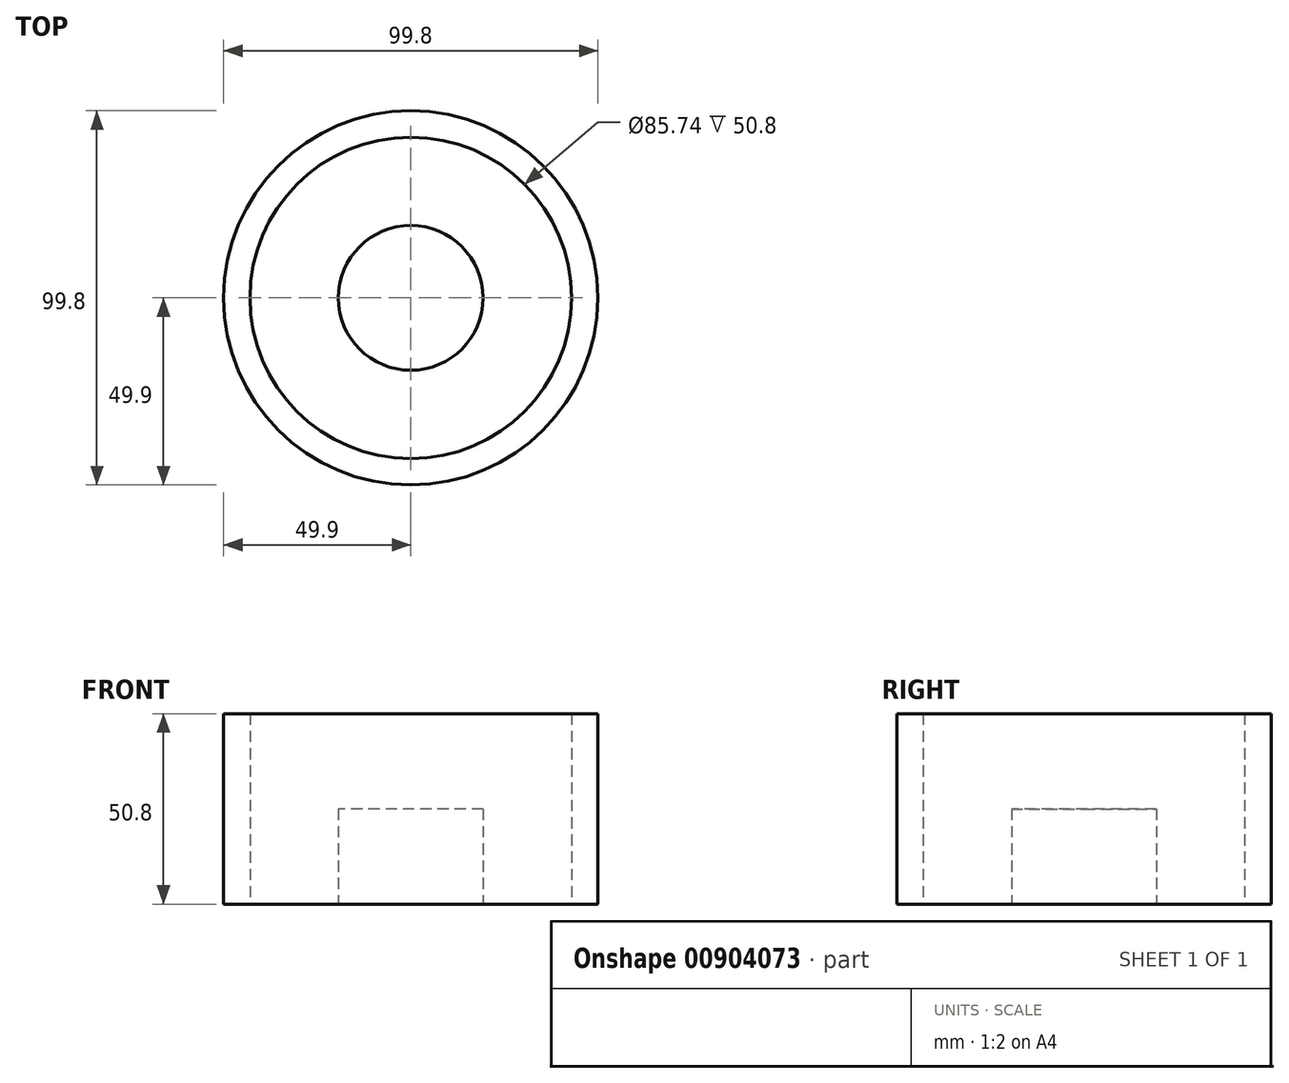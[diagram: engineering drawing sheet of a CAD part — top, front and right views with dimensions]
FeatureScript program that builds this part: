
annotation { "Feature Type Name" : "Feature", "Feature Type Description" : "" }
export const myFeature = defineFeature(function(context is Context, id is Id, definition is map)
    precondition{}
    {
        {
            var Q0;
            Q0=qCreatedBy(makeId("Top.planeOp"),FACE);
            var sketch = newSketch(context, id + "F0", { "sketchPlane" : qUnion([Q0])});
            skCircle(sketch, "E0", {"center": v(0, 0) * mm, "radius": 49.9 * mm});
            skCircle(sketch, "E1", {"center": v(0, 0) * mm, "radius": 42.87 * mm});
            skCircle(sketch, "E2", {"center": v(0, 0) * mm, "radius": 41.05 * mm});
            skCircle(sketch, "E3", {"center": v(0, 0) * mm, "radius": 16.03 * mm});
            skLineSegment(sketch, "E4", {"start": v(-9.86, -12.64) * mm, "end": v(-9.86, -27.85) * mm});
            skLineSegment(sketch, "E5", {"start": v(-9.86, -27.85) * mm, "end": v(-9.86, -27.85) * mm});
            skLineSegment(sketch, "E6", {"start": v(-9.86, -27.85) * mm, "end": v(-19.15, -36.32) * mm});
            skLineSegment(sketch, "E7", {"start": v(-4.14, -15.49) * mm, "end": v(-4.14, -28.52) * mm});
            skLineSegment(sketch, "E8", {"start": v(-4.14, -28.52) * mm, "end": v(-12.6, -39.08) * mm});
            skLineSegment(sketch, "E9", {"start": v(3.8, -15.57) * mm, "end": v(3.8, -28.58) * mm});
            skLineSegment(sketch, "E10", {"start": v(3.8, -28.58) * mm, "end": v(10.38, -39.72) * mm});
            skLineSegment(sketch, "E11", {"start": v(9.25, -13.1) * mm, "end": v(9.25, -28.58) * mm});
            skLineSegment(sketch, "E12", {"start": v(9.25, -28.58) * mm, "end": v(16.01, -37.8) * mm});
            skLineSegment(sketch, "E13", {"start": v(13.32, -8.92) * mm, "end": v(21.17, -21.55) * mm});
            skLineSegment(sketch, "E14", {"start": v(21.17, -21.55) * mm, "end": v(21.17, -35.17) * mm});
            skLineSegment(sketch, "E15", {"start": v(15.73, -3.09) * mm, "end": v(26.7, -20.26) * mm});
            skLineSegment(sketch, "E16", {"start": v(26.7, -20.26) * mm, "end": v(26.7, -31.18) * mm});
            skLineSegment(sketch, "E17", {"start": v(15.66, 3.43) * mm, "end": v(28.87, 3.43) * mm});
            skLineSegment(sketch, "E18", {"start": v(28.87, 3.43) * mm, "end": v(39.62, -10.74) * mm});
            skLineSegment(sketch, "E19", {"start": v(15.73, -3.09) * mm, "end": v(13.45, 8.72) * mm});
            skLineSegment(sketch, "E20", {"start": v(13.45, 8.72) * mm, "end": v(34.25, 8.72) * mm});
            skPoint(sketch, "E21", {"position": v(34.25, -3.65) * mm});
            skSolve(sketch);
        }
        {
            var Q0;
            Q0 = qSketchRegion(id + "F2SUZc8287iaiIb_0", true);
            var Q1;
            Q1=makeQuery(id+"F0.imprint","IMPRINT",FACE,{"disambiguationData":[TD([[makeQuery(id+"F0.imprint","IMPRINT",EDGE,{"derivedFrom":sQuery(id+"F0.wireOp",EDGE,"E0")}),1.0]])]});
            extrude(context, id + "F1", {"entities" : qUnion([Q0, Q1]), "depth" : 50.8 * mm, "offsetDistance" : 25.4 * mm});
        }
        {
            var Q0;
            Q0=qCreatedBy(makeId("Top.planeOp"),FACE);
            var sketch = newSketch(context, id + "F2", { "sketchPlane" : qUnion([Q0])});
            skCircle(sketch, "E22", {"center": v(0, 0) * mm, "radius": 40.63 * mm});
            skCircle(sketch, "E23", {"center": v(0, 0) * mm, "radius": 19.31 * mm});
            skSolve(sketch);
        }
        {
            var Q0;
            Q0=makeQuery(id+"F2.imprint","IMPRINT",FACE,{"disambiguationData":[TD([[makeQuery(id+"F2.imprint","IMPRINT",EDGE,{"derivedFrom":sQuery(id+"F2.wireOp",EDGE,"E23")}),1.0]])]});
            extrude(context, id + "F3", {"entities" : qUnion([Q0]), "depth" : 25.4 * mm, "offsetDistance" : 25.4 * mm});
        }
    });
